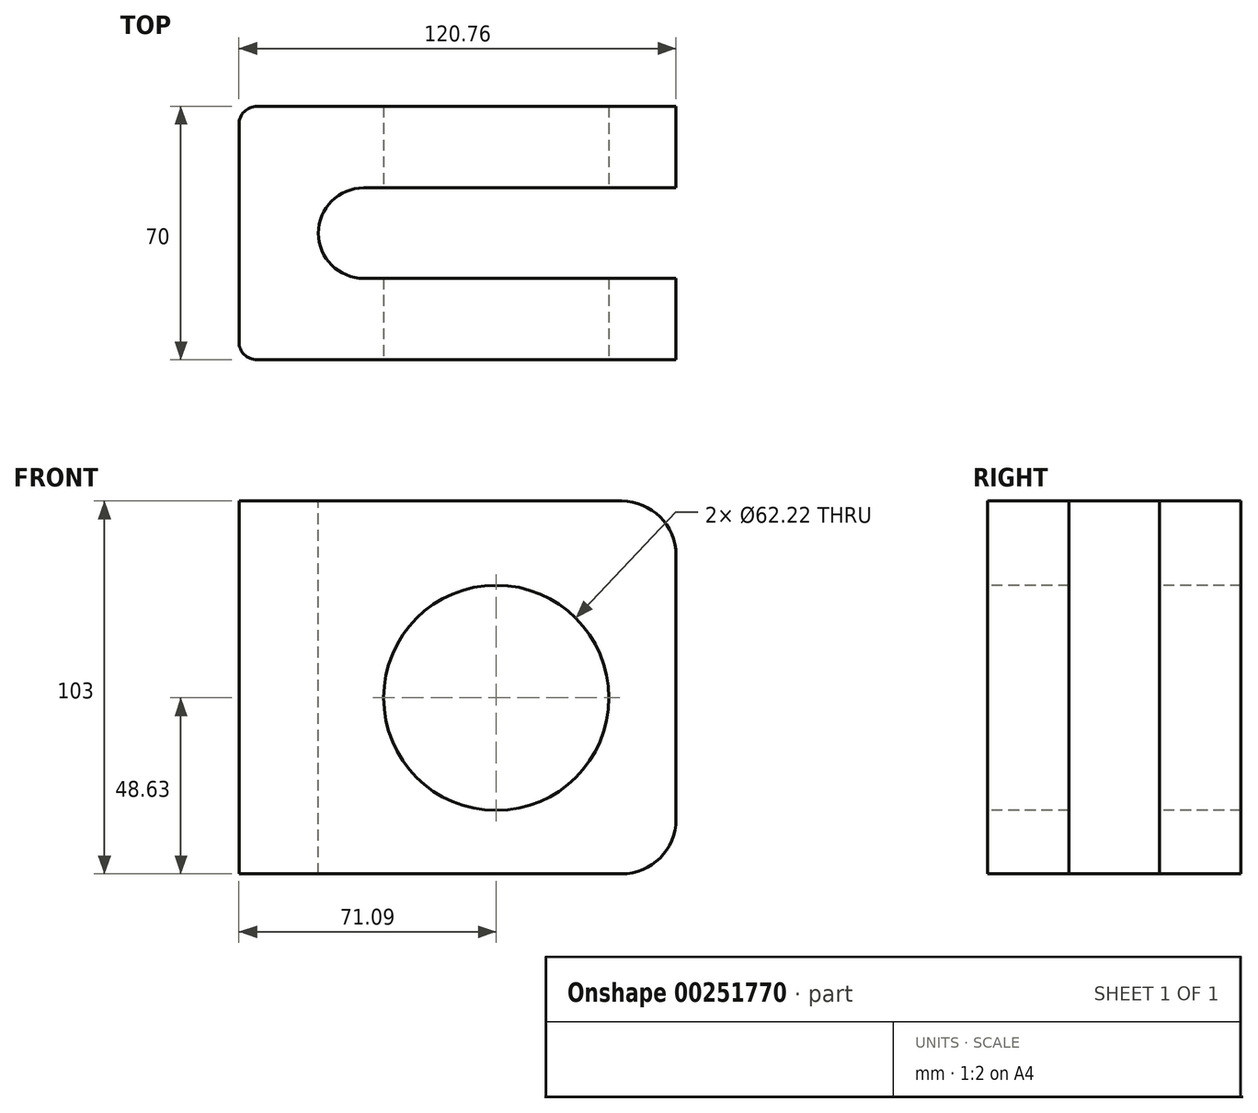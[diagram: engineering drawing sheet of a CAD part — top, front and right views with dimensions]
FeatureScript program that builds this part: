
annotation { "Feature Type Name" : "Feature", "Feature Type Description" : "" }
export const myFeature = defineFeature(function(context is Context, id is Id, definition is map)
    precondition{}
    {
        {
            var Q0;
            Q0=qCreatedBy(makeId("Front.planeOp"),FACE);
            var sketch = newSketch(context, id + "F0", { "sketchPlane" : qUnion([Q0])});
            skLineSegment(sketch, "E0", {"start": v(-71.09, 54.37) * mm, "end": v(34.67, 54.37) * mm});
            skLineSegment(sketch, "E1", {"start": v(-71.09, -48.63) * mm, "end": v(34.67, -48.63) * mm});
            skArc(sketch, "E2", {"start": v(49.67, 39.37) * mm, "mid": v(45.27, 49.97) * mm, "end": v(34.67, 54.37) * mm});
            skArc(sketch, "E3", {"start": v(34.67, -48.63) * mm, "mid": v(45.27, -44.24) * mm, "end": v(49.67, -33.63) * mm});
            skLineSegment(sketch, "E4", {"start": v(-71.09, 54.37) * mm, "end": v(-71.09, -48.63) * mm});
            skLineSegment(sketch, "E5.trimOffspring", {"start": v(49.67, 39.37) * mm, "end": v(49.67, -33.63) * mm});
            skPoint(sketch, "E6.end.orphan", {"position": v(49.67, 54.37) * mm});
            skPoint(sketch, "E6.start.orphan", {"position": v(49.67, 76.53) * mm});
            skSolve(sketch);
        }
        {
            var Q0;
            Q0=makeQuery(id+"F0.imprint","IMPRINT",FACE,{"disambiguationData":[TD([[makeQuery(id+"F0.imprint","IMPRINT",EDGE,{"derivedFrom":sQuery(id+"F0.wireOp",EDGE,"E0")}),-1.0]])]});
            extrude(context, id + "F1", {"entities" : qUnion([Q0]), "oppositeDirection" : true, "depth" : 70 * mm});
        }
        {
            var Q0;
            Q0=makeQuery(id+"F1.opExtrude","CAP_EDGE",EDGE,{"disambiguationData":[OSD([sQuery(id+"F0.wireOp",EDGE,"E4")])],"isStart":true});
            var Q1;
            Q1=makeQuery(id+"F1.opExtrude","CAP_EDGE",EDGE,{"disambiguationData":[OSD([sQuery(id+"F0.wireOp",EDGE,"E4")])],"isStart":false});
            fillet(context, id + "F2", {"entities" : qUnion([Q0, Q1]), "radius" : 5 * mm, "tangentPropagation" : true, "allowEdgeOverflow" : false});
        }
        {
            var Q0;
            Q0=makeQuery(id+"F1.opExtrude","SWEPT_FACE",FACE,{"disambiguationData":[OSD([sQuery(id+"F0.wireOp",EDGE,"E0")])]});
            var sketch = newSketch(context, id + "F3", { "sketchPlane" : qUnion([Q0])});
            skLineSegment(sketch, "E7", {"start": v(-36.62, 47.5) * mm, "end": v(71.02, 47.5) * mm});
            skLineSegment(sketch, "E8", {"start": v(71.02, 47.5) * mm, "end": v(71.02, 22.5) * mm});
            skLineSegment(sketch, "E9", {"start": v(71.02, 22.5) * mm, "end": v(-36.62, 22.5) * mm});
            skArc(sketch, "E10", {"start": v(-36.62, 47.5) * mm, "mid": v(-49.12, 35) * mm, "end": v(-36.62, 22.5) * mm});
            skPoint(sketch, "E10.centerSnap0", {"position": v(-71.09, 35) * mm});
            skSolve(sketch);
        }
        {
            var Q0;
            {var subQ0=sQuery(id+"F3.wireOp",EDGE,"E10");Q0=makeQuery(id+"F3.imprint","IMPRINT",FACE,{"disambiguationData":[TD([[makeQuery(id+"F3.imprint","IMPRINT",EDGE,{"derivedFrom":subQ0}),1.0]])]});}
            var Q1;
            {var subQ0=sQuery(id+"F3.wireOp",EDGE,"E8");Q1=makeQuery(id+"F3.imprint","IMPRINT",FACE,{"disambiguationData":[TD([[makeQuery(id+"F3.imprint","IMPRINT",EDGE,{"derivedFrom":subQ0}),-1.0]])]});}
            extrude(context, id + "F4", {"entities" : qUnion([Q0, Q1]), "operationType" : NewBodyOperationType.REMOVE, "endBound" : BoundingType.THROUGH_ALL, "oppositeDirection" : true, "depth" : 25 * mm});
        }
        {
            var Q0;
            Q0=makeQuery(id+"F1.opExtrude","CAP_FACE",FACE,{"disambiguationData":[OSD([sQuery(id+"F0.wireOp",EDGE,"E0"),sQuery(id+"F0.wireOp",EDGE,"E1"),sQuery(id+"F0.wireOp",EDGE,"E2"),sQuery(id+"F0.wireOp",EDGE,"E3"),sQuery(id+"F0.wireOp",EDGE,"E4"),sQuery(id+"F0.wireOp",EDGE,"E5.trimOffspring")])],"isStart":true});
            var sketch = newSketch(context, id + "F5", { "sketchPlane" : qUnion([Q0])});
            skCircle(sketch, "E11", {"center": v(0, 0) * mm, "radius": 31.1 * mm});
            skSolve(sketch);
        }
        {
            var Q0;
            Q0 = qSketchRegion(id + "F5", true);
            extrude(context, id + "F6", {"entities" : qUnion([Q0]), "operationType" : NewBodyOperationType.REMOVE, "endBound" : BoundingType.THROUGH_ALL, "oppositeDirection" : true, "depth" : 25 * mm});
        }
    });
